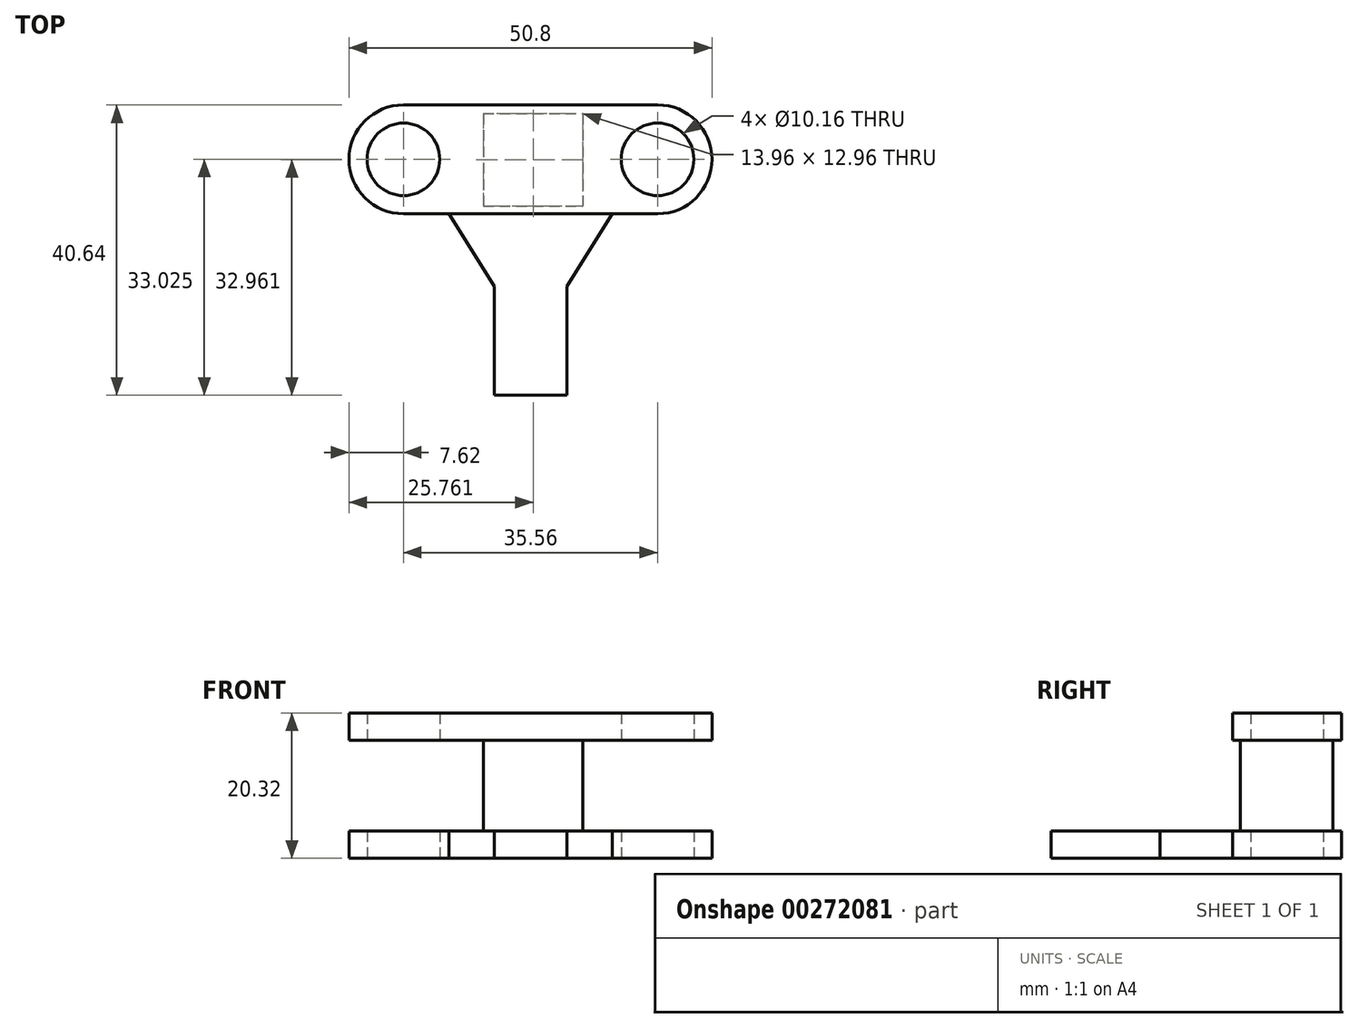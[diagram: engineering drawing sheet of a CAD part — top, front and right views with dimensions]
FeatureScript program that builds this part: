
annotation { "Feature Type Name" : "Feature", "Feature Type Description" : "" }
export const myFeature = defineFeature(function(context is Context, id is Id, definition is map)
    precondition{}
    {
        {
            var Q0;
            Q0=qCreatedBy(makeId("Top.planeOp"),FACE);
            var sketch = newSketch(context, id + "F0", { "sketchPlane" : qUnion([Q0])});
            skLineSegment(sketch, "E0.bottom", {"start": v(-17.78, 7.51) * mm, "end": v(17.78, 7.51) * mm});
            skLineSegment(sketch, "E0.top", {"start": v(-17.78, -7.73) * mm, "end": v(17.78, -7.73) * mm});
            skArc(sketch, "E1", {"start": v(-17.78, 7.51) * mm, "mid": v(-25.4, -0.1) * mm, "end": v(-17.78, -7.73) * mm});
            skArc(sketch, "E2", {"start": v(17.78, -7.73) * mm, "mid": v(25.4, -0.1) * mm, "end": v(17.78, 7.51) * mm});
            skCircle(sketch, "E3", {"center": v(-17.78, -0.1) * mm, "radius": 5.08 * mm});
            skCircle(sketch, "E4", {"center": v(17.78, -0.1) * mm, "radius": 5.08 * mm});
            skLineSegment(sketch, "E5.bottom", {"start": v(-5.08, -7.73) * mm, "end": v(5.08, -7.73) * mm});
            skLineSegment(sketch, "E5.top", {"start": v(-5.08, -33.13) * mm, "end": v(5.08, -33.13) * mm});
            skLineSegment(sketch, "E5.left", {"start": v(-5.08, -7.73) * mm, "end": v(-5.08, -33.13) * mm});
            skLineSegment(sketch, "E5.right", {"start": v(5.08, -7.73) * mm, "end": v(5.08, -33.13) * mm});
            skLineSegment(sketch, "E6", {"start": v(0, -7.73) * mm, "end": v(0, 0) * mm});
            skLineSegment(sketch, "E7", {"start": v(-11.43, -7.73) * mm, "end": v(-5.08, -17.89) * mm});
            skLineSegment(sketch, "E8", {"start": v(11.43, -7.73) * mm, "end": v(5.08, -17.89) * mm});
            skLineSegment(sketch, "E9", {"start": v(-5.08, -17.89) * mm, "end": v(5.08, -17.89) * mm});
            skSolve(sketch);
        }
        {
            var Q0;
            Q0 = qSketchRegion(id + "F0", true);
            extrude(context, id + "F1", {"entities" : qUnion([Q0]), "depth" : 3.8 * mm});
        }
        {
            var Q0;
            Q0=makeQuery(id+"F1.opExtrude","CAP_FACE",FACE,{"disambiguationData":[OSD([sQuery(id+"F0.wireOp",EDGE,"E0.bottom"),sQuery(id+"F0.wireOp",EDGE,"E0.top"),sQuery(id+"F0.wireOp",EDGE,"E1"),sQuery(id+"F0.wireOp",EDGE,"E2"),sQuery(id+"F0.wireOp",EDGE,"E3"),sQuery(id+"F0.wireOp",EDGE,"E4"),sQuery(id+"F0.wireOp",EDGE,"E5.top"),sQuery(id+"F0.wireOp",EDGE,"E5.left"),sQuery(id+"F0.wireOp",EDGE,"E5.right"),sQuery(id+"F0.wireOp",EDGE,"E7"),sQuery(id+"F0.wireOp",EDGE,"E8")])],"isStart":false});
            var sketch = newSketch(context, id + "F2", { "sketchPlane" : qUnion([Q0])});
            skLineSegment(sketch, "E10.bottom", {"start": v(-6.62, 6.3) * mm, "end": v(7.34, 6.3) * mm});
            skLineSegment(sketch, "E10.top", {"start": v(-6.62, -6.65) * mm, "end": v(7.34, -6.65) * mm});
            skLineSegment(sketch, "E10.left", {"start": v(-6.62, 6.3) * mm, "end": v(-6.62, -6.65) * mm});
            skLineSegment(sketch, "E10.right", {"start": v(7.34, 6.3) * mm, "end": v(7.34, -6.65) * mm});
            skSolve(sketch);
        }
        {
            var Q0;
            Q0 = qSketchRegion(id + "F2", true);
            extrude(context, id + "F3", {"entities" : qUnion([Q0]), "operationType" : NewBodyOperationType.ADD, "depth" : 12.7 * mm});
        }
        {
            var Q0;
            Q0=makeQuery(id+"F3.opExtrude","CAP_FACE",FACE,{"disambiguationData":[OSD([sQuery(id+"F2.wireOp",EDGE,"E10.bottom"),sQuery(id+"F2.wireOp",EDGE,"E10.top"),sQuery(id+"F2.wireOp",EDGE,"E10.left"),sQuery(id+"F2.wireOp",EDGE,"E10.right")])],"isStart":false});
            var sketch = newSketch(context, id + "F4", { "sketchPlane" : qUnion([Q0])});
            skCircle(sketch, "E11.0", {"center": v(-17.78, -0.1) * mm, "radius": 5.08 * mm});
            skLineSegment(sketch, "E11.1", {"start": v(-17.78, 7.51) * mm, "end": v(17.78, 7.51) * mm});
            skArc(sketch, "E11.2", {"start": v(-17.78, 7.51) * mm, "mid": v(-25.4, -0.1) * mm, "end": v(-17.78, -7.73) * mm});
            skLineSegment(sketch, "E11.3", {"start": v(-17.78, -7.73) * mm, "end": v(-11.43, -7.73) * mm});
            skLineSegment(sketch, "E11.4", {"start": v(11.43, -7.73) * mm, "end": v(17.78, -7.73) * mm});
            skArc(sketch, "E11.5", {"start": v(17.78, -7.73) * mm, "mid": v(25.4, -0.1) * mm, "end": v(17.78, 7.51) * mm});
            skCircle(sketch, "E11.6", {"center": v(17.78, -0.1) * mm, "radius": 5.08 * mm});
            skLineSegment(sketch, "E12", {"start": v(-11.43, -7.73) * mm, "end": v(11.43, -7.73) * mm});
            skSolve(sketch);
        }
        {
            var Q0;
            Q0 = qSketchRegion(id + "F4", true);
            extrude(context, id + "F5", {"entities" : qUnion([Q0]), "operationType" : NewBodyOperationType.ADD, "depth" : 3.8 * mm});
        }
    });
